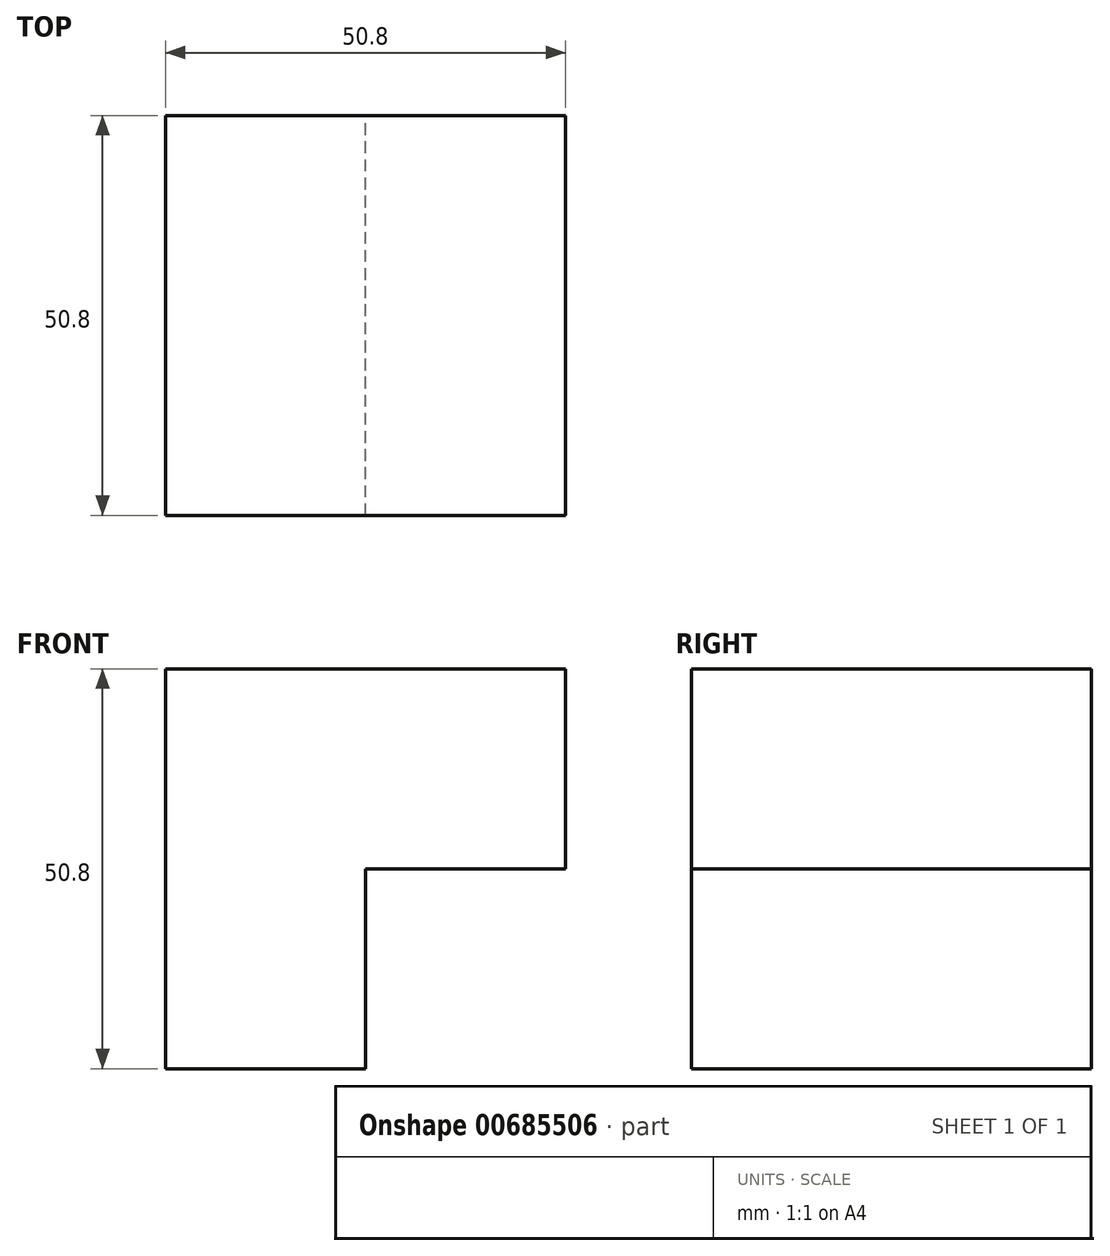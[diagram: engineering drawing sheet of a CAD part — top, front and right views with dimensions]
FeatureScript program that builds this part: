
annotation { "Feature Type Name" : "Feature", "Feature Type Description" : "" }
export const myFeature = defineFeature(function(context is Context, id is Id, definition is map)
    precondition{}
    {
        {
            var Q0;
            Q0=qCreatedBy(makeId("Front.planeOp"),FACE);
            var sketch = newSketch(context, id + "F0", { "sketchPlane" : qUnion([Q0])});
            skLineSegment(sketch, "E0.bottom", {"start": v(0, 0) * mm, "end": v(-50.8, 0) * mm});
            skLineSegment(sketch, "E0.top", {"start": v(0, 50.8) * mm, "end": v(-50.8, 50.8) * mm});
            skLineSegment(sketch, "E0.left", {"start": v(0, 0) * mm, "end": v(0, 50.8) * mm});
            skLineSegment(sketch, "E0.right", {"start": v(-50.8, 0) * mm, "end": v(-50.8, 50.8) * mm});
            skSolve(sketch);
        }
        {
            var Q0;
            Q0=makeQuery(id+"F0.imprint","IMPRINT",FACE,{"disambiguationData":[TD([[makeQuery(id+"F0.imprint","IMPRINT",EDGE,{"derivedFrom":sQuery(id+"F0.wireOp",EDGE,"E0.bottom")}),-1.0]])]});
            var sketch = newSketch(context, id + "F1", { "sketchPlane" : qUnion([Q0])});
            skLineSegment(sketch, "E1.bottom", {"start": v(0, 0) * mm, "end": v(-25.4, 0) * mm});
            skLineSegment(sketch, "E1.top", {"start": v(0, 25.4) * mm, "end": v(-25.4, 25.4) * mm});
            skLineSegment(sketch, "E1.left", {"start": v(0, 0) * mm, "end": v(0, 25.4) * mm});
            skLineSegment(sketch, "E1.right", {"start": v(-25.4, 0) * mm, "end": v(-25.4, 25.4) * mm});
            skSolve(sketch);
        }
        {
            var Q0;
            Q0 = qSketchRegion(id + "F0", true);
            extrude(context, id + "F2", {"entities" : qUnion([Q0]), "depth" : 50.8 * mm, "offsetDistance" : 25.4 * mm});
        }
        {
            var Q0;
            Q0 = qSketchRegion(id + "F1", true);
            extrude(context, id + "F3", {"entities" : qUnion([Q0]), "operationType" : NewBodyOperationType.REMOVE, "depth" : 50.8 * mm, "offsetDistance" : 25.4 * mm});
        }
    });
